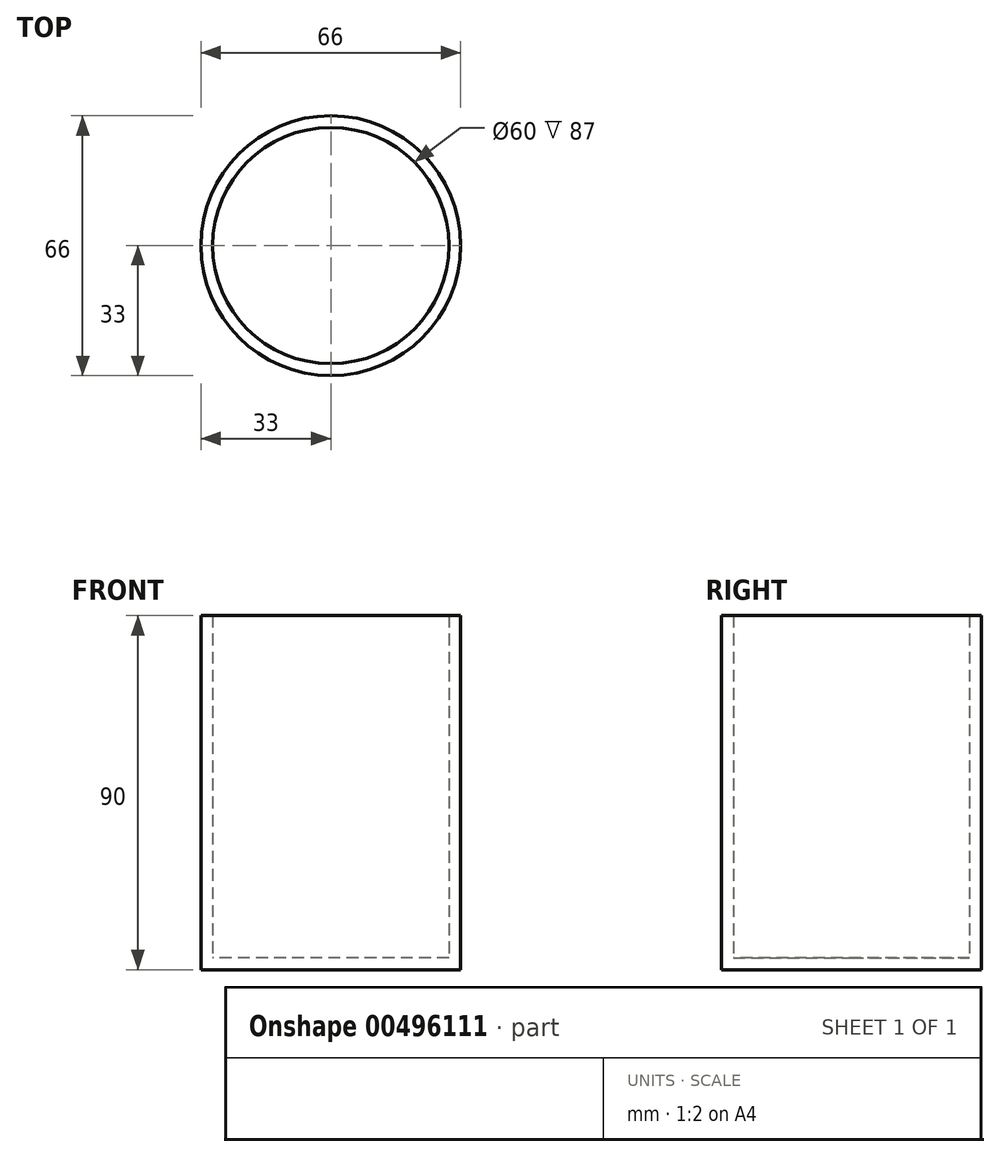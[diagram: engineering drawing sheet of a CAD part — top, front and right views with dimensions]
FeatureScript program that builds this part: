
annotation { "Feature Type Name" : "Feature", "Feature Type Description" : "" }
export const myFeature = defineFeature(function(context is Context, id is Id, definition is map)
    precondition{}
    {
        {
            var Q0;
            Q0=qCreatedBy(makeId("Top.planeOp"),FACE);
            var sketch = newSketch(context, id + "F0", { "sketchPlane" : qUnion([Q0])});
            skCircle(sketch, "E0", {"center": v(0, 0) * mm, "radius": 33 * mm});
            skCircle(sketch, "E1", {"center": v(0, 0) * mm, "radius": 30 * mm});
            skSolve(sketch);
        }
        {
            var Q0;
            Q0=makeQuery(id+"F0.imprint","IMPRINT",FACE,{"disambiguationData":[TD([[makeQuery(id+"F0.imprint","IMPRINT",EDGE,{"derivedFrom":sQuery(id+"F0.wireOp",EDGE,"E1")}),1.0]])]});
            extrude(context, id + "F1", {"entities" : qUnion([Q0]), "depth" : 3 * mm});
        }
        {
            var Q0;
            Q0=qSketchRegion(id+"F0",true);
            extrude(context, id + "F2", {"entities" : qUnion([Q0]), "operationType" : NewBodyOperationType.ADD, "depth" : 90 * mm});
        }
    });
